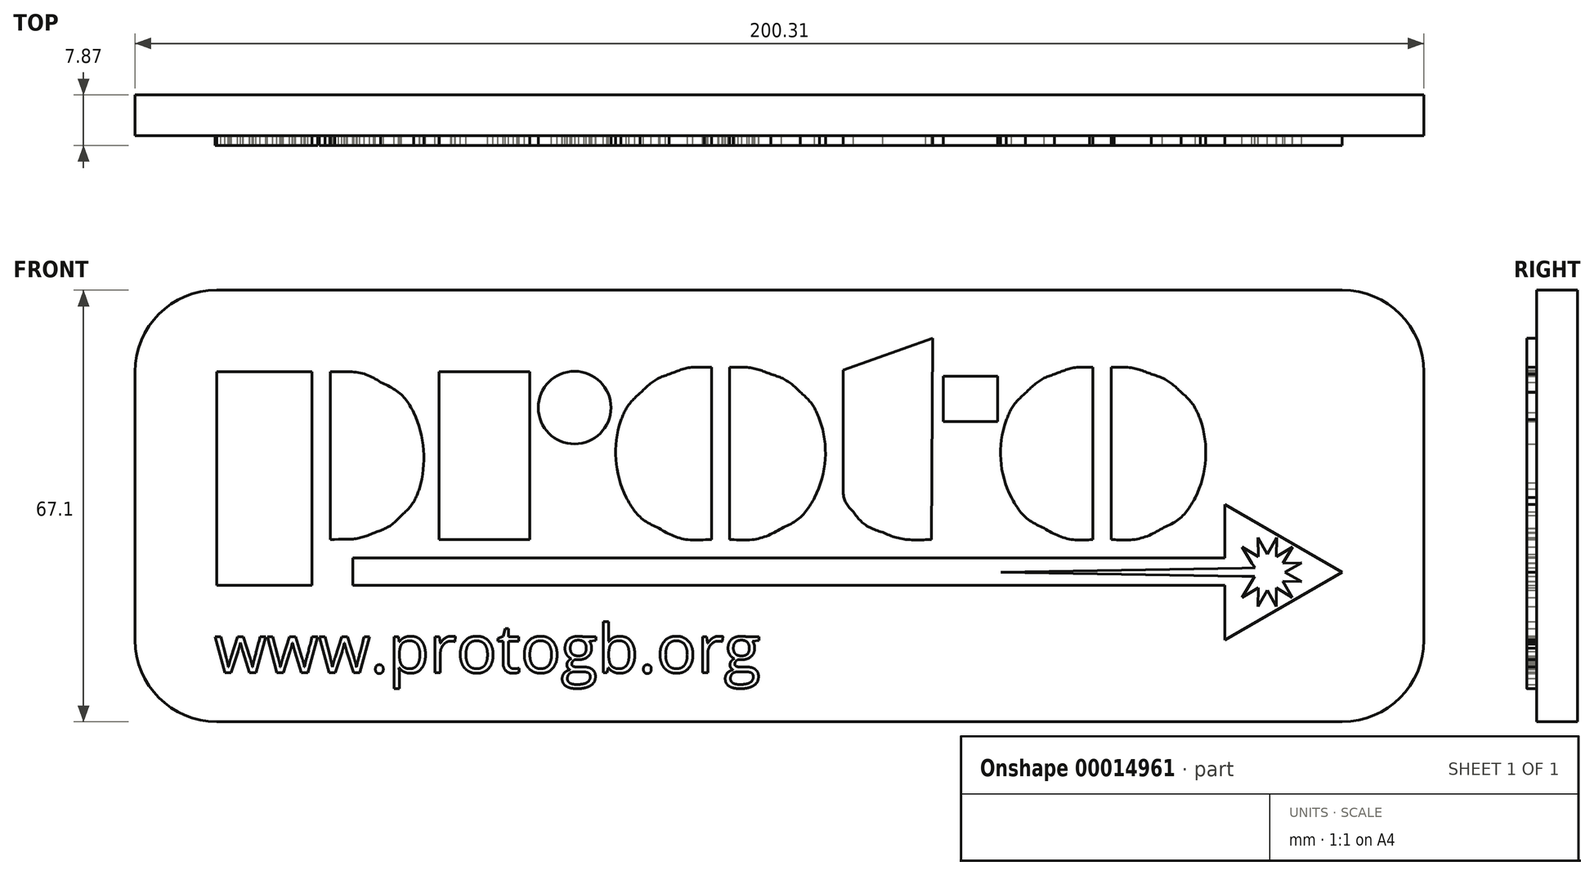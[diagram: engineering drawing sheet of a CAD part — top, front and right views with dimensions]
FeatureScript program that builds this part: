
annotation { "Feature Type Name" : "Feature", "Feature Type Description" : "" }
export const myFeature = defineFeature(function(context is Context, id is Id, definition is map)
    precondition{}
    {
        {
            var Q0;
            Q0=qCreatedBy(makeId("Front.planeOp"),FACE);
            var sketch = newSketch(context, id + "F0", { "sketchPlane" : qUnion([Q0])});
            skLineSegment(sketch, "E0", {"start": v(34.59, -11.74) * mm, "end": v(34.59, -7.47) * mm});
            skLineSegment(sketch, "E1", {"start": v(34.59, -7.47) * mm, "end": v(-33.14, -7.47) * mm});
            skLineSegment(sketch, "E2", {"start": v(-33.14, -7.47) * mm, "end": v(-33.14, -5.35) * mm});
            skLineSegment(sketch, "E3", {"start": v(-33.14, -5.35) * mm, "end": v(34.59, -5.35) * mm});
            skLineSegment(sketch, "E4", {"start": v(34.59, -5.35) * mm, "end": v(34.59, -1.19) * mm});
            skLineSegment(sketch, "E5", {"start": v(34.59, -1.19) * mm, "end": v(43.73, -6.46) * mm});
            skLineSegment(sketch, "E6", {"start": v(43.73, -6.46) * mm, "end": v(34.59, -11.74) * mm});
            skLineSegment(sketch, "E7", {"start": v(39.29, -6.47) * mm, "end": v(40.58, -5.75) * mm});
            skLineSegment(sketch, "E8", {"start": v(40.58, -5.75) * mm, "end": v(39.1, -5.77) * mm});
            skLineSegment(sketch, "E9", {"start": v(39.1, -5.77) * mm, "end": v(39.86, -4.5) * mm});
            skLineSegment(sketch, "E10", {"start": v(39.86, -4.5) * mm, "end": v(38.6, -5.26) * mm});
            skLineSegment(sketch, "E11", {"start": v(38.6, -5.26) * mm, "end": v(38.62, -3.78) * mm});
            skLineSegment(sketch, "E12", {"start": v(38.62, -3.78) * mm, "end": v(37.9, -5.08) * mm});
            skLineSegment(sketch, "E13", {"start": v(37.9, -5.08) * mm, "end": v(37.19, -3.78) * mm});
            skLineSegment(sketch, "E14", {"start": v(37.19, -3.78) * mm, "end": v(37.2, -5.26) * mm});
            skLineSegment(sketch, "E15", {"start": v(37.2, -5.26) * mm, "end": v(35.94, -4.5) * mm});
            skLineSegment(sketch, "E16", {"start": v(35.94, -4.5) * mm, "end": v(36.7, -5.77) * mm});
            skLineSegment(sketch, "E17", {"start": v(36.7, -5.77) * mm, "end": v(36.94, -6.13) * mm});
            skLineSegment(sketch, "E18", {"start": v(36.94, -6.13) * mm, "end": v(35.95, -6.15) * mm});
            skLineSegment(sketch, "E19", {"start": v(35.95, -6.15) * mm, "end": v(17.22, -6.47) * mm});
            skLineSegment(sketch, "E20", {"start": v(17.22, -6.47) * mm, "end": v(35.92, -6.78) * mm});
            skLineSegment(sketch, "E21", {"start": v(35.92, -6.78) * mm, "end": v(36.92, -6.79) * mm});
            skLineSegment(sketch, "E22", {"start": v(36.92, -6.79) * mm, "end": v(36.7, -7.15) * mm});
            skLineSegment(sketch, "E23", {"start": v(36.7, -7.15) * mm, "end": v(35.93, -8.42) * mm});
            skLineSegment(sketch, "E24", {"start": v(35.93, -8.42) * mm, "end": v(37.2, -7.66) * mm});
            skLineSegment(sketch, "E25", {"start": v(37.2, -7.66) * mm, "end": v(37.18, -9.14) * mm});
            skLineSegment(sketch, "E26", {"start": v(37.18, -9.14) * mm, "end": v(37.9, -7.85) * mm});
            skLineSegment(sketch, "E27", {"start": v(37.9, -7.85) * mm, "end": v(38.61, -9.14) * mm});
            skLineSegment(sketch, "E28", {"start": v(38.61, -9.14) * mm, "end": v(38.6, -7.67) * mm});
            skLineSegment(sketch, "E29", {"start": v(38.6, -7.67) * mm, "end": v(39.86, -8.43) * mm});
            skLineSegment(sketch, "E30", {"start": v(39.86, -8.43) * mm, "end": v(39.1, -7.16) * mm});
            skLineSegment(sketch, "E31", {"start": v(39.1, -7.16) * mm, "end": v(40.58, -7.19) * mm});
            skLineSegment(sketch, "E32", {"start": v(40.58, -7.19) * mm, "end": v(39.29, -6.47) * mm});
            skFitSpline(sketch, "E33", {"points": [v(24.17, -3.94) * mm, v(22.86, -3.94) * mm, v(21.66, -3.63) * mm, v(20.57, -3.05) * mm]});
            skFitSpline(sketch, "E34", {"points": [v(20.57, -3.05) * mm, v(19.5, -2.48) * mm, v(18.64, -1.67) * mm, v(18.02, -0.65) * mm]});
            skFitSpline(sketch, "E35", {"points": [v(17.61, 5.34) * mm, v(17.96, 6.13) * mm, v(18.46, 6.84) * mm, v(19.11, 7.47) * mm]});
            skFitSpline(sketch, "E36", {"points": [v(19.11, 7.47) * mm, v(19.77, 8.08) * mm, v(20.51, 8.6) * mm, v(21.36, 8.92) * mm]});
            skFitSpline(sketch, "E37", {"points": [v(21.36, 8.92) * mm, v(22.21, 9.25) * mm, v(23.13, 9.47) * mm, v(24.1, 9.47) * mm]});
            skFitSpline(sketch, "E38", {"points": [v(25.98, 9.47) * mm, v(27.05, 9.47) * mm, v(28.02, 9.26) * mm, v(28.9, 8.94) * mm]});
            skFitSpline(sketch, "E39", {"points": [v(28.9, 8.94) * mm, v(29.8, 8.6) * mm, v(30.57, 8.12) * mm, v(31.2, 7.54) * mm]});
            skFitSpline(sketch, "E40", {"points": [v(31.2, 7.54) * mm, v(31.84, 6.94) * mm, v(32.34, 6.21) * mm, v(32.7, 5.4) * mm]});
            skFitSpline(sketch, "E41", {"points": [v(32.3, -0.67) * mm, v(31.7, -1.66) * mm, v(30.83, -2.48) * mm, v(29.74, -3.06) * mm]});
            skFitSpline(sketch, "E42", {"points": [v(29.74, -3.06) * mm, v(28.65, -3.63) * mm, v(27.42, -3.94) * mm, v(26.05, -3.94) * mm]});
            skLineSegment(sketch, "E43", {"start": v(16.95, 5.23) * mm, "end": v(12.72, 5.23) * mm});
            skLineSegment(sketch, "E44", {"start": v(12.72, 5.23) * mm, "end": v(12.72, 8.76) * mm});
            skLineSegment(sketch, "E45", {"start": v(12.72, 8.76) * mm, "end": v(16.95, 8.76) * mm});
            skLineSegment(sketch, "E46", {"start": v(16.95, 8.76) * mm, "end": v(16.95, 5.23) * mm});
            skFitSpline(sketch, "E47", {"points": [v(-3.6, 9.47) * mm, v(-2.53, 9.47) * mm, v(-1.56, 9.26) * mm, v(-0.68, 8.94) * mm]});
            skFitSpline(sketch, "E48", {"points": [v(-0.68, 8.94) * mm, v(0.22, 8.6) * mm, v(0.99, 8.12) * mm, v(1.61, 7.54) * mm]});
            skFitSpline(sketch, "E49", {"points": [v(1.61, 7.54) * mm, v(2.26, 6.94) * mm, v(2.76, 6.21) * mm, v(3.12, 5.4) * mm]});
            skFitSpline(sketch, "E50", {"points": [v(2.73, -0.67) * mm, v(2.11, -1.66) * mm, v(1.25, -2.48) * mm, v(0.16, -3.06) * mm]});
            skFitSpline(sketch, "E51", {"points": [v(0.16, -3.06) * mm, v(-0.93, -3.63) * mm, v(-2.16, -3.94) * mm, v(-3.53, -3.94) * mm]});
            skFitSpline(sketch, "E52", {"points": [v(-5.76, -3.94) * mm, v(-7.08, -3.94) * mm, v(-8.28, -3.63) * mm, v(-9.37, -3.05) * mm]});
            skFitSpline(sketch, "E53", {"points": [v(-9.37, -3.05) * mm, v(-10.44, -2.48) * mm, v(-11.3, -1.67) * mm, v(-11.91, -0.65) * mm]});
            skFitSpline(sketch, "E54", {"points": [v(-12.32, 5.34) * mm, v(-11.97, 6.13) * mm, v(-11.47, 6.84) * mm, v(-10.82, 7.47) * mm]});
            skFitSpline(sketch, "E55", {"points": [v(-10.82, 7.47) * mm, v(-10.17, 8.08) * mm, v(-9.42, 8.6) * mm, v(-8.58, 8.92) * mm]});
            skFitSpline(sketch, "E56", {"points": [v(-8.58, 8.92) * mm, v(-7.72, 9.25) * mm, v(-6.8, 9.47) * mm, v(-5.84, 9.47) * mm]});
            skFitSpline(sketch, "E57", {"points": [v(-34.54, 9.11) * mm, v(-33.26, 9.11) * mm, v(-32.07, 8.89) * mm, v(-30.98, 8.3) * mm]});
            skFitSpline(sketch, "E58", {"points": [v(-30.98, 8.3) * mm, v(-29.9, 7.74) * mm, v(-29.04, 6.98) * mm, v(-28.42, 5.96) * mm]});
            skFitSpline(sketch, "E59", {"points": [v(-27.98, 0.02) * mm, v(-28.3, -0.77) * mm, v(-28.77, -1.46) * mm, v(-29.37, -2.05) * mm]});
            skFitSpline(sketch, "E60", {"points": [v(-29.37, -2.05) * mm, v(-29.97, -2.64) * mm, v(-30.69, -3.1) * mm, v(-31.53, -3.4) * mm]});
            skFitSpline(sketch, "E61", {"points": [v(-31.53, -3.4) * mm, v(-32.36, -3.73) * mm, v(-33.27, -3.9) * mm, v(-34.26, -3.9) * mm]});
            skLineSegment(sketch, "E62", {"start": v(-43.73, -7.47) * mm, "end": v(-43.73, 9.11) * mm});
            skLineSegment(sketch, "E63", {"start": v(-43.73, 9.11) * mm, "end": v(-36.32, 9.11) * mm});
            skLineSegment(sketch, "E64", {"start": v(-36.32, 9.11) * mm, "end": v(-36.32, -7.47) * mm});
            skLineSegment(sketch, "E65", {"start": v(-36.32, -7.47) * mm, "end": v(-43.73, -7.47) * mm});
            skLineSegment(sketch, "E66", {"start": v(-19.39, -3.94) * mm, "end": v(-26.44, -3.94) * mm});
            skLineSegment(sketch, "E67", {"start": v(-26.44, -3.94) * mm, "end": v(-26.44, 9.11) * mm});
            skLineSegment(sketch, "E68", {"start": v(-26.44, 9.11) * mm, "end": v(-19.39, 9.11) * mm});
            skLineSegment(sketch, "E69", {"start": v(-19.39, 9.11) * mm, "end": v(-19.39, -3.94) * mm});
            skFitSpline(sketch, "E70", {"points": [v(11.36, -3.94) * mm, v(10.12, -3.94) * mm, v(9, -3.75) * mm, v(8.01, -3.36) * mm]});
            skFitSpline(sketch, "E71", {"points": [v(8.01, -3.36) * mm, v(7, -2.97) * mm, v(6.28, -2.44) * mm, v(5.74, -1.77) * mm]});
            skFitSpline(sketch, "E72", {"points": [v(5.74, -1.77) * mm, v(5.17, -1.1) * mm, v(4.96, -0.34) * mm, v(4.96, 0.5) * mm]});
            skLineSegment(sketch, "E73", {"start": v(4.96, 0.5) * mm, "end": v(4.96, 9.24) * mm});
            skLineSegment(sketch, "E74", {"start": v(4.96, 9.24) * mm, "end": v(11.89, 11.74) * mm});
            skLineSegment(sketch, "E75", {"start": v(11.89, 11.74) * mm, "end": v(11.8, -3.94) * mm});
            skLineSegment(sketch, "E76", {"start": v(11.8, -3.94) * mm, "end": v(11.36, -3.94) * mm});
            skLineSegment(sketch, "E77", {"start": v(-34.54, 9.11) * mm, "end": v(-34.9, 9.11) * mm});
            skLineSegment(sketch, "E78", {"start": v(-34.9, -3.94) * mm, "end": v(-34.57, -3.94) * mm});
            skLineSegment(sketch, "E79", {"start": v(-34.9, 9.11) * mm, "end": v(-34.9, -3.94) * mm});
            skLineSegment(sketch, "E80", {"start": v(-34.26, -3.9) * mm, "end": v(-34.57, -3.94) * mm});
            skArc(sketch, "E81", {"start": v(-27.98, 0.02) * mm, "mid": v(-27.65, 3.03) * mm, "end": v(-28.42, 5.96) * mm});
            skCircle(sketch, "E82", {"center": v(-15.92, 6.33) * mm, "radius": 2.82 * mm});
            skArc(sketch, "E83", {"start": v(-12.32, 5.34) * mm, "mid": v(-12.71, 2.3) * mm, "end": v(-11.91, -0.65) * mm});
            skArc(sketch, "E84", {"start": v(2.73, -0.67) * mm, "mid": v(3.56, 2.32) * mm, "end": v(3.12, 5.4) * mm});
            skLineSegment(sketch, "E85", {"start": v(-5.28, 9.47) * mm, "end": v(-5.28, -3.94) * mm});
            skLineSegment(sketch, "E86", {"start": v(-3.86, -3.94) * mm, "end": v(-3.86, 9.47) * mm});
            skLineSegment(sketch, "E87", {"start": v(-5.84, 9.47) * mm, "end": v(-5.28, 9.47) * mm});
            skLineSegment(sketch, "E88", {"start": v(-3.86, 9.47) * mm, "end": v(-3.6, 9.47) * mm});
            skLineSegment(sketch, "E89", {"start": v(-5.76, -3.94) * mm, "end": v(-5.28, -3.94) * mm});
            skLineSegment(sketch, "E90", {"start": v(-3.86, -3.94) * mm, "end": v(-3.53, -3.94) * mm});
            skLineSegment(sketch, "E91", {"start": v(24.36, 9.47) * mm, "end": v(24.36, -3.94) * mm});
            skLineSegment(sketch, "E92", {"start": v(25.77, -3.94) * mm, "end": v(25.77, 9.47) * mm});
            skLineSegment(sketch, "E93", {"start": v(24.1, 9.47) * mm, "end": v(24.36, 9.47) * mm});
            skLineSegment(sketch, "E94", {"start": v(25.77, 9.47) * mm, "end": v(25.98, 9.47) * mm});
            skLineSegment(sketch, "E95", {"start": v(24.17, -3.94) * mm, "end": v(24.36, -3.94) * mm});
            skLineSegment(sketch, "E96", {"start": v(25.77, -3.94) * mm, "end": v(26.05, -3.94) * mm});
            skArc(sketch, "E97", {"start": v(17.61, 5.34) * mm, "mid": v(17.2, 2.3) * mm, "end": v(18.02, -0.65) * mm});
            skArc(sketch, "E98", {"start": v(32.3, -0.67) * mm, "mid": v(33.1, 2.33) * mm, "end": v(32.7, 5.4) * mm});
            skSolve(sketch);
        }
        {
            var Q0;
            Q0=qCreatedBy(makeId("Front.planeOp"),FACE);
            var sketch = newSketch(context, id + "F1", { "sketchPlane" : qUnion([Q0])});
            skLineSegment(sketch, "E99.bottom", {"start": v(-50.08, -18.09) * mm, "end": v(50.08, -18.09) * mm});
            skLineSegment(sketch, "E99.top", {"start": v(-50.08, 15.46) * mm, "end": v(50.08, 15.46) * mm});
            skLineSegment(sketch, "E99.left", {"start": v(-50.08, -18.09) * mm, "end": v(-50.08, 15.46) * mm});
            skLineSegment(sketch, "E99.right", {"start": v(50.08, -18.09) * mm, "end": v(50.08, 15.46) * mm});
            skSolve(sketch);
        }
        {
            var Q0;
            Q0=makeQuery(id+"F1.imprint","IMPRINT",FACE,{"disambiguationData":[TD([[makeQuery(id+"F1.imprint","IMPRINT",EDGE,{"derivedFrom":sQuery(id+"F1.wireOp",EDGE,"E99.bottom")}),1.0]])]});
            extrude(context, id + "F2", {"entities" : qUnion([Q0]), "oppositeDirection" : true, "depth" : 3.17 * mm});
        }
        {
            var Q0;
            Q0=makeQuery(id+"F0.imprint","IMPRINT",FACE,{"disambiguationData":[TD([[makeQuery(id+"F0.imprint","IMPRINT",EDGE,{"derivedFrom":sQuery(id+"F0.wireOp",EDGE,"E62")}),-1.0]])]});
            var Q1;
            Q1=makeQuery(id+"F0.imprint","IMPRINT",FACE,{"disambiguationData":[TD([[makeQuery(id+"F0.imprint","IMPRINT",EDGE,{"derivedFrom":sQuery(id+"F0.wireOp",EDGE,"E57")}),-1.0]])]});
            var Q2;
            Q2=makeQuery(id+"F0.imprint","IMPRINT",FACE,{"disambiguationData":[TD([[makeQuery(id+"F0.imprint","IMPRINT",EDGE,{"derivedFrom":sQuery(id+"F0.wireOp",EDGE,"E66")}),-1.0]])]});
            var Q3;
            Q3=makeQuery(id+"F0.imprint","IMPRINT",FACE,{"disambiguationData":[TD([[makeQuery(id+"F0.imprint","IMPRINT",EDGE,{"derivedFrom":sQuery(id+"F0.wireOp",EDGE,"E82")}),1.0]])]});
            var Q4;
            Q4=makeQuery(id+"F0.imprint","IMPRINT",FACE,{"disambiguationData":[TD([[makeQuery(id+"F0.imprint","IMPRINT",EDGE,{"derivedFrom":sQuery(id+"F0.wireOp",EDGE,"E52")}),-1.0]])]});
            var Q5;
            Q5=makeQuery(id+"F0.imprint","IMPRINT",FACE,{"disambiguationData":[TD([[makeQuery(id+"F0.imprint","IMPRINT",EDGE,{"derivedFrom":sQuery(id+"F0.wireOp",EDGE,"E47")}),-1.0]])]});
            var Q6;
            Q6=makeQuery(id+"F0.imprint","IMPRINT",FACE,{"disambiguationData":[TD([[makeQuery(id+"F0.imprint","IMPRINT",EDGE,{"derivedFrom":sQuery(id+"F0.wireOp",EDGE,"E70")}),-1.0]])]});
            var Q7;
            Q7=makeQuery(id+"F0.imprint","IMPRINT",FACE,{"disambiguationData":[TD([[makeQuery(id+"F0.imprint","IMPRINT",EDGE,{"derivedFrom":sQuery(id+"F0.wireOp",EDGE,"E43")}),-1.0]])]});
            var Q8;
            Q8=makeQuery(id+"F0.imprint","IMPRINT",FACE,{"disambiguationData":[TD([[makeQuery(id+"F0.imprint","IMPRINT",EDGE,{"derivedFrom":sQuery(id+"F0.wireOp",EDGE,"E33")}),-1.0]])]});
            var Q9;
            Q9=makeQuery(id+"F0.imprint","IMPRINT",FACE,{"disambiguationData":[TD([[makeQuery(id+"F0.imprint","IMPRINT",EDGE,{"derivedFrom":sQuery(id+"F0.wireOp",EDGE,"E38")}),-1.0]])]});
            var Q10;
            Q10=makeQuery(id+"F0.imprint","IMPRINT",FACE,{"disambiguationData":[TD([[makeQuery(id+"F0.imprint","IMPRINT",EDGE,{"derivedFrom":sQuery(id+"F0.wireOp",EDGE,"E0")}),-1.0]])]});
            extrude(context, id + "F3", {"entities" : qUnion([Q0, Q1, Q2, Q3, Q4, Q5, Q6, Q7, Q8, Q9, Q10]), "operationType" : NewBodyOperationType.ADD, "depth" : 0.76 * mm});
        }
        {
            var Q0;
            {var subQ0=sQuery(id+"F1.wireOp",EDGE,"E99.bottom");var subQ1=sQuery(id+"F1.wireOp",EDGE,"E99.top");var subQ2=sQuery(id+"F1.wireOp",EDGE,"E99.left");var subQ3=sQuery(id+"F1.wireOp",EDGE,"E99.right");Q0=makeQuery(id+"F3.boolean.opBoolean","SPLIT",FACE,{"disambiguationData":[TD([makeQuery(id+"F2.opExtrude","SWEPT_FACE",FACE,{"disambiguationData":[OSD([subQ0])]})])],"derivedFrom":makeQuery(id+"F2.opExtrude","CAP_FACE",FACE,{"disambiguationData":[OSD([subQ0,subQ1,subQ2,subQ3])],"isStart":true})});}
            var sketch = newSketch(context, id + "F4", { "sketchPlane" : qUnion([Q0])});
            skText(sketch, "E100", { "text": "www.protogb.org", "fontName": "OpenSans-Regular.ttf"});
            const initialGuessF4  = {"E100": [-0.0439, -0.01427, 1, 0, 0.00374]};
            skSetInitialGuess(sketch, initialGuessF4);
            skSolve(sketch);
        }
        {
            var Q0;
            Q0 = qSketchRegion(id + "F4", true);
            var Q1;
            Q1=makeQuery(id+"F3.opExtrude","CAP_FACE",FACE,{"disambiguationData":[OSD([sQuery(id+"F0.wireOp",EDGE,"E62"),sQuery(id+"F0.wireOp",EDGE,"E63"),sQuery(id+"F0.wireOp",EDGE,"E64"),sQuery(id+"F0.wireOp",EDGE,"E65")])],"isStart":false});
            extrude(context, id + "F5", {"entities" : qUnion([Q0]), "operationType" : NewBodyOperationType.ADD, "endBoundEntityFace" : qUnion([Q1]), "depth" : 0.76 * mm});
        }
        {
            var Q0;
            Q0=makeQuery(id+"F2.opExtrude","SWEPT_BODY",BODY,{"disambiguationData":[OSD([sQuery(id+"F1.wireOp",EDGE,"E99.bottom"),sQuery(id+"F1.wireOp",EDGE,"E99.top"),sQuery(id+"F1.wireOp",EDGE,"E99.left"),sQuery(id+"F1.wireOp",EDGE,"E99.right")])]});
            var Q1;
            Q1=makeQuery(id+"F2.opExtrude","CAP_VERTEX",VERTEX,{"disambiguationData":[OSD([sQuery(id+"F1.wireOp",EDGE,"E99.top"),sQuery(id+"F1.wireOp",EDGE,"E99.left")])],"isStart":true});
            transform(context, id + "F6", {"entities" : qUnion([Q0]), "transformType" : TransformType.SCALE_UNIFORMLY, "scale" : 2, "makeCopy" : false, "scalePoint" : qUnion([Q1])});
        }
        {
            var Q0;
            Q0=makeQuery(id+"F2.opExtrude","SWEPT_EDGE",EDGE,{"disambiguationData":[OSD([sQuery(id+"F1.wireOp",EDGE,"E99.top"),sQuery(id+"F1.wireOp",EDGE,"E99.right")])]});
            var Q1;
            Q1=makeQuery(id+"F2.opExtrude","SWEPT_EDGE",EDGE,{"disambiguationData":[OSD([sQuery(id+"F1.wireOp",EDGE,"E99.bottom"),sQuery(id+"F1.wireOp",EDGE,"E99.right")])]});
            var Q2;
            Q2=makeQuery(id+"F2.opExtrude","SWEPT_EDGE",EDGE,{"disambiguationData":[OSD([sQuery(id+"F1.wireOp",EDGE,"E99.top"),sQuery(id+"F1.wireOp",EDGE,"E99.left")])]});
            var Q3;
            Q3=makeQuery(id+"F2.opExtrude","SWEPT_EDGE",EDGE,{"disambiguationData":[OSD([sQuery(id+"F1.wireOp",EDGE,"E99.bottom"),sQuery(id+"F1.wireOp",EDGE,"E99.left")])]});
            fillet(context, id + "F7", {"entities" : qUnion([Q0, Q1, Q2, Q3]), "radius" : 12.7 * mm, "tangentPropagation" : true, "allowEdgeOverflow" : false});
        }
    });
